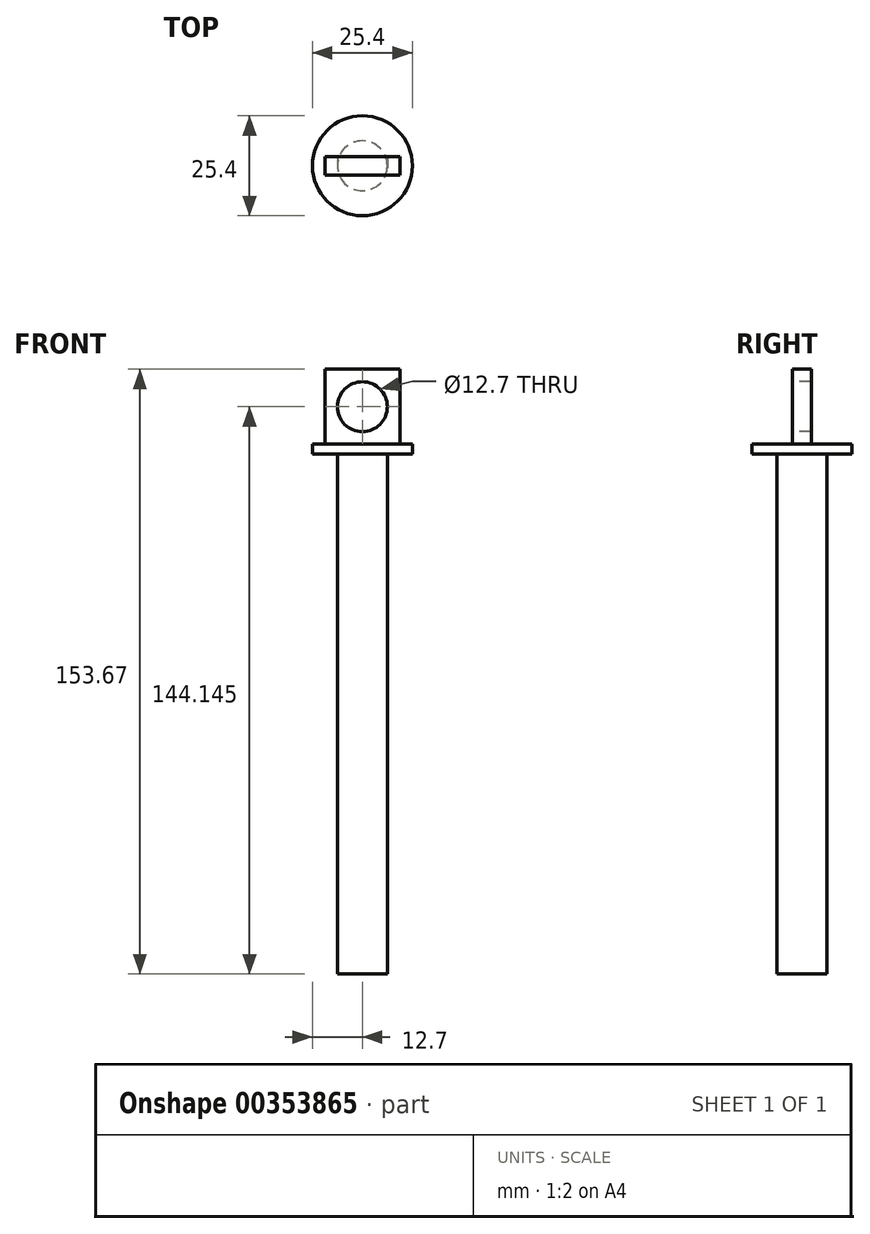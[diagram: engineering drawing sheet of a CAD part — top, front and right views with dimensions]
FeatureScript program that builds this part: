
annotation { "Feature Type Name" : "Feature", "Feature Type Description" : "" }
export const myFeature = defineFeature(function(context is Context, id is Id, definition is map)
    precondition{}
    {
        {
            var Q0;
            Q0=qCreatedBy(makeId("Top.planeOp"),FACE);
            var sketch = newSketch(context, id + "F0", { "sketchPlane" : qUnion([Q0])});
            skCircle(sketch, "E0", {"center": v(0, 0) * mm, "radius": 6.35 * mm});
            skSolve(sketch);
        }
        {
            var Q0;
            Q0 = qSketchRegion(id + "F0", true);
            extrude(context, id + "F1", {"entities" : qUnion([Q0]), "depth" : 132.08 * mm});
        }
        {
            var Q0;
            Q0=makeQuery(id+"F1.opExtrude","CAP_FACE",FACE,{"disambiguationData":[OSD([sQuery(id+"F0.wireOp",EDGE,"E0")])],"isStart":false});
            var sketch = newSketch(context, id + "F2", { "sketchPlane" : qUnion([Q0])});
            skCircle(sketch, "E1", {"center": v(0, 0) * mm, "radius": 12.7 * mm});
            skSolve(sketch);
        }
        {
            var Q0;
            Q0 = qSketchRegion(id + "F2", true);
            extrude(context, id + "F3", {"entities" : qUnion([Q0]), "operationType" : NewBodyOperationType.ADD, "depth" : 2.54 * mm});
        }
        {
            var Q0;
            Q0=qCreatedBy(makeId("Front.planeOp"),FACE);
            var sketch = newSketch(context, id + "F4", { "sketchPlane" : qUnion([Q0])});
            skLineSegment(sketch, "E2", {"start": v(0, 0) * mm, "end": v(0, 144.15) * mm, "construction": true});
            skCircle(sketch, "E3.cCircle", {"center": v(0, 144.15) * mm, "radius": 13.47 * mm, "construction": true});
            skLineSegment(sketch, "E3.0", {"start": v(-9.53, 134.62) * mm, "end": v(-9.53, 153.67) * mm});
            skLineSegment(sketch, "E3.1", {"start": v(-9.53, 153.67) * mm, "end": v(9.52, 153.67) * mm});
            skLineSegment(sketch, "E3.2", {"start": v(9.52, 153.67) * mm, "end": v(9.52, 134.62) * mm});
            skLineSegment(sketch, "E3.3", {"start": v(9.53, 134.62) * mm, "end": v(-9.53, 134.62) * mm});
            skSolve(sketch);
        }
        {
            var Q0;
            Q0 = qSketchRegion(id + "F4", true);
            extrude(context, id + "F5", {"entities" : qUnion([Q0]), "operationType" : NewBodyOperationType.ADD, "endBound" : BoundingType.SYMMETRIC, "depth" : 4.76 * mm});
        }
        {
            var Q0;
            Q0=makeQuery(id+"F5.opExtrude","CAP_FACE",FACE,{"disambiguationData":[OSD([sQuery(id+"F4.wireOp",EDGE,"E3.0"),sQuery(id+"F4.wireOp",EDGE,"E3.1"),sQuery(id+"F4.wireOp",EDGE,"E3.2"),sQuery(id+"F4.wireOp",EDGE,"E3.3")])],"isStart":false});
            var sketch = newSketch(context, id + "F6", { "sketchPlane" : qUnion([Q0])});
            skCircle(sketch, "E4", {"center": v(0, 144.15) * mm, "radius": 6.35 * mm});
            skSolve(sketch);
        }
        {
            var Q0;
            Q0 = qSketchRegion(id + "F6", true);
            extrude(context, id + "F7", {"entities" : qUnion([Q0]), "operationType" : NewBodyOperationType.REMOVE, "oppositeDirection" : true, "depth" : 4.76 * mm});
        }
    });
